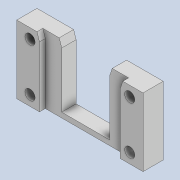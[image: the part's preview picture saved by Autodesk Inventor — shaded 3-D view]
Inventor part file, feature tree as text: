
AUTODESK INVENTOR PART (.ipt)
format: ipt  version: 2020 (Build 240168000, 168)  size: 164,864 bytes
history: native  units: mm
features: chamfer x4, sketch x4, extrude x3, other x2, hole x1, mirror x1, reference x1
ambient origin geometry x8: Origin, YZ Plane, XZ Plane, XY Plane, X Axis, Y Axis, Z Axis, Center Point
bodies: Solid1 (feature_tree)
feature tree (16):
  extrude  "Extrusion1"  Depth=50.0mm
  extrude  "Extrusion2"  Depth=19.0mm
  extrude  "Extrusion3"  Depth=3.0mm TaperAngle=0.0deg
  hole  "Hole1"  [1 undecoded]
  mirror  "Mirror1"
  chamfer  "Chamfer1"  Distance=5.0mm
  chamfer  "Chamfer2"  Distance=2.3mm
  chamfer  "Chamfer3"  Distance=5.25mm
  chamfer  "Chamfer4"  Distance=4.0mm
  sketch  "Sketch1"  dims[d0=27.0mm d1=50.0mm]
  sketch  "Sketch2"  dims[d2=8.0mm d3=0.0mm d4=19.0mm]
  sketch  "Sketch3"  dims[d5=2.0mm d6=3.0mm d7=0.0mm]
  reference  "Reference1"
  sketch  "Sketch4"  dims[d8=6.5mm d9=6.5mm d10=5.0mm d11=2.3mm d12=0.0mm d13=5.25mm d14=4.0mm d15=4.0mm d16=4.0mm d17=6.0mm d18=7.0mm d19=3.0mm d20=90.0deg d21=8.0mm d22=20.594885mm d23=1.0mm d24=3.0mm d25=45.0deg d26=1.0mm d27=3.0mm d28=45.0deg d29=1.0mm d30=3.0mm d31=45.0deg d32=1.0mm d33=3.0mm d34=45.0deg]
  other  "0008-10-10 Injectomat Standard.iam"
  other  "Body Syringe.ipt:1"
note: 1 required parameter value undecoded (feature->parameter linkage not recoverable at this tier; creation-order binding heuristic only, values carry confidence <= 0.55)
